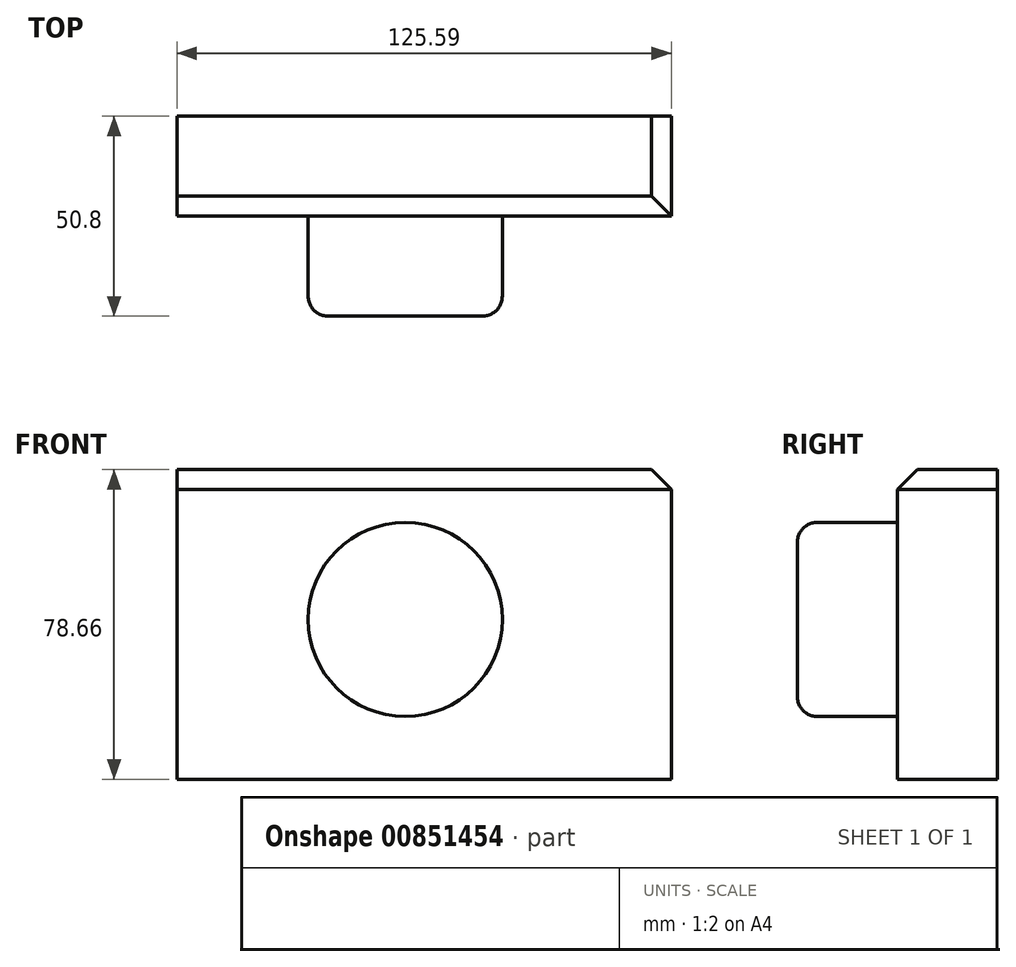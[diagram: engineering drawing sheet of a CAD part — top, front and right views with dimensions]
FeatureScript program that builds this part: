
annotation { "Feature Type Name" : "Feature", "Feature Type Description" : "" }
export const myFeature = defineFeature(function(context is Context, id is Id, definition is map)
    precondition{}
    {
        {
            var Q0;
            Q0=qCreatedBy(makeId("Front.planeOp"),FACE);
            var sketch = newSketch(context, id + "F0", { "sketchPlane" : qUnion([Q0])});
            skLineSegment(sketch, "E0.bottom", {"start": v(-58, 38.05) * mm, "end": v(67.6, 38.05) * mm});
            skLineSegment(sketch, "E0.top", {"start": v(-58, -40.61) * mm, "end": v(67.6, -40.61) * mm});
            skLineSegment(sketch, "E0.left", {"start": v(-58, 38.05) * mm, "end": v(-58, -40.61) * mm});
            skLineSegment(sketch, "E0.right", {"start": v(67.6, 38.05) * mm, "end": v(67.6, -40.61) * mm});
            skSolve(sketch);
        }
        {
            var Q0;
            Q0 = qSketchRegion(id + "F0", true);
            extrude(context, id + "F1", {"entities" : qUnion([Q0]), "depth" : 25.4 * mm, "offsetDistance" : 25.4 * mm});
        }
        {
            var Q0;
            Q0=makeQuery(id+"F1.opExtrude","SWEPT_EDGE",EDGE,{"disambiguationData":[OSD([sQuery(id+"F0.wireOp",EDGE,"E0.bottom"),sQuery(id+"F0.wireOp",EDGE,"E0.right")])]});
            var Q1;
            Q1=makeQuery(id+"F1.opExtrude","CAP_EDGE",EDGE,{"disambiguationData":[OSD([sQuery(id+"F0.wireOp",EDGE,"E0.bottom")])],"isStart":false});
            chamfer(context, id + "F2", {"entities" : qUnion([Q0, Q1]), "width" : 5.08 * mm, "tangentPropagation" : true});
        }
        {
            var Q0;
            Q0=makeQuery(id+"F1.opExtrude","CAP_FACE",FACE,{"disambiguationData":[OSD([sQuery(id+"F0.wireOp",EDGE,"E0.bottom"),sQuery(id+"F0.wireOp",EDGE,"E0.top"),sQuery(id+"F0.wireOp",EDGE,"E0.left"),sQuery(id+"F0.wireOp",EDGE,"E0.right")])],"isStart":false});
            var sketch = newSketch(context, id + "F3", { "sketchPlane" : qUnion([Q0])});
            skCircle(sketch, "E1", {"center": v(0, 0) * mm, "radius": 24.65 * mm});
            skSolve(sketch);
        }
        {
            var Q0;
            Q0 = qSketchRegion(id + "F3", true);
            extrude(context, id + "F4", {"entities" : qUnion([Q0]), "operationType" : NewBodyOperationType.ADD, "depth" : 25.4 * mm, "offsetDistance" : 25.4 * mm});
        }
        {
            var Q0;
            Q0=makeQuery(id+"F4.opExtrude","CAP_EDGE",EDGE,{"disambiguationData":[OSD([sQuery(id+"F3.wireOp",EDGE,"E1")])],"isStart":false});
            fillet(context, id + "F5", {"entities" : qUnion([Q0]), "radius" : 5.08 * mm, "tangentPropagation" : true, "allowEdgeOverflow" : false});
        }
    });
